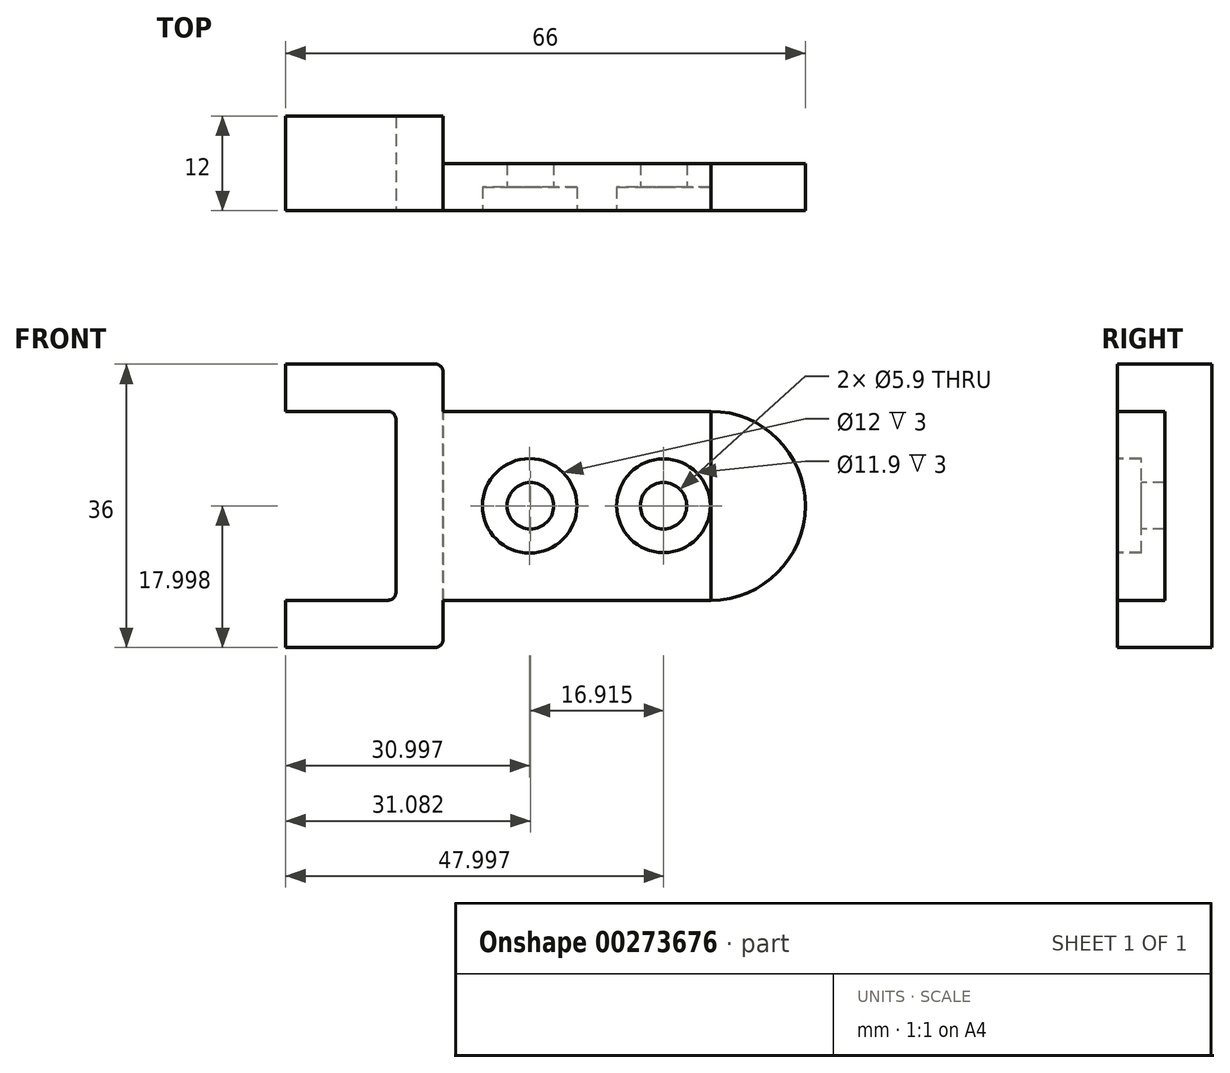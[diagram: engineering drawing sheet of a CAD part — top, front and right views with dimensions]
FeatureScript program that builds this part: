
annotation { "Feature Type Name" : "Feature", "Feature Type Description" : "" }
export const myFeature = defineFeature(function(context is Context, id is Id, definition is map)
    precondition{}
    {
        {
            var Q0;
            Q0=qCreatedBy(makeId("Front.planeOp"),FACE);
            var sketch = newSketch(context, id + "F0", { "sketchPlane" : qUnion([Q0])});
            skLineSegment(sketch, "E0.bottom", {"start": v(-41.74, 12.9) * mm, "end": v(-21.74, 12.9) * mm});
            skLineSegment(sketch, "E0.top", {"start": v(-41.74, -23.1) * mm, "end": v(-21.74, -23.1) * mm});
            skLineSegment(sketch, "E0.left", {"start": v(-41.74, 12.9) * mm, "end": v(-41.74, -23.1) * mm});
            skLineSegment(sketch, "E0.right", {"start": v(-21.74, 12.9) * mm, "end": v(-21.74, -23.1) * mm});
            skSolve(sketch);
        }
        {
            var Q0;
            Q0=makeQuery(id+"F0.imprint","IMPRINT",FACE,{"disambiguationData":[TD([[makeQuery(id+"F0.imprint","IMPRINT",EDGE,{"derivedFrom":sQuery(id+"F0.wireOp",EDGE,"E0.bottom")}),-1.0]])]});
            extrude(context, id + "F1", {"entities" : qUnion([Q0]), "depth" : 12 * mm});
        }
        {
            var Q0;
            Q0=makeQuery(id+"F1.opExtrude","SWEPT_FACE",FACE,{"disambiguationData":[OSD([sQuery(id+"F0.wireOp",EDGE,"E0.left")])]});
            var sketch = newSketch(context, id + "F2", { "sketchPlane" : qUnion([Q0])});
            skLineSegment(sketch, "E1.bottom", {"start": v(0, -17.1) * mm, "end": v(12, -17.1) * mm});
            skLineSegment(sketch, "E1.top", {"start": v(0, 6.9) * mm, "end": v(12, 6.9) * mm});
            skLineSegment(sketch, "E1.left", {"start": v(0, -17.1) * mm, "end": v(0, 6.9) * mm});
            skLineSegment(sketch, "E1.right", {"start": v(12, -17.1) * mm, "end": v(12, 6.9) * mm});
            skPoint(sketch, "E1.middle", {"position": v(6, -5.1) * mm});
            skPoint(sketch, "E1.middle.positionSnap0", {"position": v(12, -5.1) * mm});
            skPoint(sketch, "E1.middle.positionSnap1", {"position": v(6, -23.1) * mm});
            skPoint(sketch, "E1.centerSnap0", {"position": v(12, -5.1) * mm});
            skPoint(sketch, "E1.centerSnap1", {"position": v(6, -23.1) * mm});
            skSolve(sketch);
        }
        {
            var Q0;
            Q0=makeQuery(id+"F2.imprint","IMPRINT",FACE,{"disambiguationData":[TD([[makeQuery(id+"F2.imprint","IMPRINT",EDGE,{"derivedFrom":sQuery(id+"F2.wireOp",EDGE,"E1.bottom")}),1.0]])]});
            extrude(context, id + "F3", {"entities" : qUnion([Q0]), "operationType" : NewBodyOperationType.REMOVE, "oppositeDirection" : true, "depth" : 14 * mm});
        }
        {
            var Q0;
            Q0=qCreatedBy(makeId("Right.planeOp"),FACE);
            var sketch = newSketch(context, id + "F4", { "sketchPlane" : qUnion([Q0])});
            skLineSegment(sketch, "E2", {"start": v(-12.14, -23.1) * mm, "end": v(-12.14, -17.1) * mm});
            skLineSegment(sketch, "E3", {"start": v(-12.14, 12.8) * mm, "end": v(-12.14, 6.8) * mm});
            skLineSegment(sketch, "E4.bottom", {"start": v(-12.14, -17.1) * mm, "end": v(-6.14, -17.1) * mm});
            skLineSegment(sketch, "E4.top", {"start": v(-12.14, 6.8) * mm, "end": v(-6.14, 6.8) * mm});
            skLineSegment(sketch, "E4.left", {"start": v(-12.14, -17.1) * mm, "end": v(-12.14, 6.8) * mm});
            skLineSegment(sketch, "E4.right", {"start": v(-6.14, -17.1) * mm, "end": v(-6.14, 6.8) * mm});
            skSolve(sketch);
        }
        {
            var Q0;
            Q0=makeQuery(id+"F4.imprint","IMPRINT",FACE,{"disambiguationData":[TD([[makeQuery(id+"F4.imprint","IMPRINT",EDGE,{"derivedFrom":sQuery(id+"F4.wireOp",EDGE,"E4.bottom")}),1.0]])]});
            extrude(context, id + "F5", {"entities" : qUnion([Q0]), "depth" : 34 * mm});
        }
        {
            var Q0;
            Q0=makeQuery(id+"F5.opExtrude","SWEPT_BODY",BODY,{"disambiguationData":[OSD([sQuery(id+"F4.wireOp",EDGE,"E4.bottom"),sQuery(id+"F4.wireOp",EDGE,"E4.top"),sQuery(id+"F4.wireOp",EDGE,"E4.left"),sQuery(id+"F4.wireOp",EDGE,"E4.right")])]});
            deleteBodies(context, id + "F6", {"entities" : qUnion([Q0])});
        }
        {
            var Q0;
            Q0=makeQuery(id+"F1.opExtrude","SWEPT_FACE",FACE,{"disambiguationData":[OSD([sQuery(id+"F0.wireOp",EDGE,"E0.right")])]});
            var sketch = newSketch(context, id + "F7", { "sketchPlane" : qUnion([Q0])});
            skLineSegment(sketch, "E5", {"start": v(-12, -17.1) * mm, "end": v(-12, 6.9) * mm});
            skLineSegment(sketch, "E6", {"start": v(-12, -17.1) * mm, "end": v(-6, -17.1) * mm});
            skLineSegment(sketch, "E7", {"start": v(-12, 6.9) * mm, "end": v(-6, 6.9) * mm});
            skLineSegment(sketch, "E8", {"start": v(-6, -17.1) * mm, "end": v(-6, 6.9) * mm});
            skSolve(sketch);
        }
        {
            var Q0;
            Q0=makeQuery(id+"F7.imprint","IMPRINT",FACE,{"disambiguationData":[TD([[makeQuery(id+"F7.imprint","IMPRINT",EDGE,{"derivedFrom":sQuery(id+"F7.wireOp",EDGE,"E5")}),1.0]])]});
            extrude(context, id + "F8", {"entities" : qUnion([Q0]), "operationType" : NewBodyOperationType.ADD, "depth" : 34 * mm});
        }
        {
            var Q0;
            Q0=makeQuery(id+"F8.opExtrude","SWEPT_FACE",FACE,{"disambiguationData":[OSD([sQuery(id+"F7.wireOp",EDGE,"E8")])]});
            var sketch = newSketch(context, id + "F9", { "sketchPlane" : qUnion([Q0])});
            skArc(sketch, "E9", {"start": v(-12.26, 6.9) * mm, "mid": v(-24.26, -5.1) * mm, "end": v(-12.26, -17.1) * mm});
            skSolve(sketch);
        }
        {
            var Q0;
            Q0=makeQuery(id+"F9.imprint","IMPRINT",FACE,{"disambiguationData":[TD([[makeQuery(id+"F9.imprint","IMPRINT",EDGE,{"derivedFrom":sQuery(id+"F9.wireOp",EDGE,"E9")}),1.0]])]});
            extrude(context, id + "F10", {"entities" : qUnion([Q0]), "oppositeDirection" : true, "depth" : 6 * mm});
        }
        {
            var Q0;
            Q0=makeQuery(id+"F8.boolean.opBoolean","MERGE",FACE,{"derivedFrom":[makeQuery(id+"F1.opExtrude","CAP_FACE",FACE,{"disambiguationData":[OSD([sQuery(id+"F0.wireOp",EDGE,"E0.bottom"),sQuery(id+"F0.wireOp",EDGE,"E0.top"),sQuery(id+"F0.wireOp",EDGE,"E0.left"),sQuery(id+"F0.wireOp",EDGE,"E0.right")])],"isStart":false}),makeQuery(id+"F8.opExtrude","SWEPT_FACE",FACE,{"disambiguationData":[OSD([sQuery(id+"F7.wireOp",EDGE,"E5")])]})]});
            var sketch = newSketch(context, id + "F11", { "sketchPlane" : qUnion([Q0])});
            skCircle(sketch, "E10", {"center": v(-10.74, -5.1) * mm, "radius": 6 * mm});
            skPoint(sketch, "E11.orphan", {"position": v(-27.74, -5.1) * mm});
            skSolve(sketch);
        }
        {
            var Q0;
            Q0=makeQuery(id+"F11.imprint","IMPRINT",FACE,{"disambiguationData":[TD([[makeQuery(id+"F11.imprint","IMPRINT",EDGE,{"derivedFrom":sQuery(id+"F11.wireOp",EDGE,"E10")}),1.0]])]});
            extrude(context, id + "F12", {"entities" : qUnion([Q0]), "operationType" : NewBodyOperationType.REMOVE, "oppositeDirection" : true, "depth" : 3 * mm});
        }
        {
            var Q0;
            Q0=makeQuery(id+"F8.boolean.opBoolean","MERGE",FACE,{"derivedFrom":[makeQuery(id+"F1.opExtrude","CAP_FACE",FACE,{"disambiguationData":[OSD([sQuery(id+"F0.wireOp",EDGE,"E0.bottom"),sQuery(id+"F0.wireOp",EDGE,"E0.top"),sQuery(id+"F0.wireOp",EDGE,"E0.left"),sQuery(id+"F0.wireOp",EDGE,"E0.right")])],"isStart":false}),makeQuery(id+"F8.opExtrude","SWEPT_FACE",FACE,{"disambiguationData":[OSD([sQuery(id+"F7.wireOp",EDGE,"E5")])]})]});
            var sketch = newSketch(context, id + "F13", { "sketchPlane" : qUnion([Q0])});
            skPoint(sketch, "E12.orphan", {"position": v(-10.74, -5.1) * mm});
            skLineSegment(sketch, "E13", {"start": v(-10.74, -5.1) * mm, "end": v(6.26, -5.1) * mm});
            skCircle(sketch, "E14", {"center": v(6.26, -5.1) * mm, "radius": 5.95 * mm});
            skSolve(sketch);
        }
        {
            var Q0;
            Q0=makeQuery(id+"F13.imprint","IMPRINT",FACE,{"disambiguationData":[TD([[makeQuery(id+"F13.imprint","IMPRINT",EDGE,{"derivedFrom":sQuery(id+"F13.wireOp",EDGE,"E14")}),1.0]])]});
            extrude(context, id + "F14", {"entities" : qUnion([Q0]), "operationType" : NewBodyOperationType.REMOVE, "oppositeDirection" : true, "depth" : 3 * mm});
        }
        {
            var Q0;
            Q0=makeQuery(id+"F14.boolean.opBoolean","COPY",FACE,{"derivedFrom":makeQuery(id+"F14.opExtrude","CAP_FACE",FACE,{"disambiguationData":[OSD([sQuery(id+"F13.wireOp",EDGE,"E14")])],"isStart":false})});
            var sketch = newSketch(context, id + "F15", { "sketchPlane" : qUnion([Q0])});
            skCircle(sketch, "E15", {"center": v(6.26, -5.1) * mm, "radius": 2.95 * mm});
            skCircle(sketch, "E16", {"center": v(-10.66, -5.1) * mm, "radius": 2.95 * mm});
            skSolve(sketch);
        }
        {
            var Q0;
            Q0=sQuery(id+"F15.wireOp",VERTEX,"E15.center");
            var Q1;
            Q1=sQuery(id+"F15.wireOp",VERTEX,"E16.center");
            var Q2;
            Q2=makeQuery(id+"F1.opExtrude","SWEPT_BODY",BODY,{"disambiguationData":[OSD([sQuery(id+"F0.wireOp",EDGE,"E0.bottom"),sQuery(id+"F0.wireOp",EDGE,"E0.top"),sQuery(id+"F0.wireOp",EDGE,"E0.left"),sQuery(id+"F0.wireOp",EDGE,"E0.right")])]});
            hole(context, id + "F16", {"style" : HoleStyle.SIMPLE, "endStyle" : HoleEndStyle.THROUGH, "holeDiameter" : 5.9 * mm, "tappedDepth" : 12 * mm, "tapClearance" : 3, "locations" : qUnion([Q0, Q1]), "scope" : qUnion([Q2])});
        }
        {
            var Q0;
            Q0=makeQuery(id+"F3.boolean.opBoolean","COPY",EDGE,{"derivedFrom":makeQuery(id+"F3.opExtrude","CAP_EDGE",EDGE,{"disambiguationData":[OSD([sQuery(id+"F2.wireOp",EDGE,"E1.top")])],"isStart":false})});
            var Q1;
            Q1=makeQuery(id+"F3.boolean.opBoolean","COPY",EDGE,{"derivedFrom":makeQuery(id+"F3.opExtrude","CAP_EDGE",EDGE,{"disambiguationData":[OSD([sQuery(id+"F2.wireOp",EDGE,"E1.bottom")])],"isStart":false})});
            var Q2;
            Q2=makeQuery(id+"F1.opExtrude","SWEPT_EDGE",EDGE,{"disambiguationData":[OSD([sQuery(id+"F0.wireOp",EDGE,"E0.bottom"),sQuery(id+"F0.wireOp",EDGE,"E0.right")])]});
            var Q3;
            Q3=makeQuery(id+"F1.opExtrude","SWEPT_EDGE",EDGE,{"disambiguationData":[OSD([sQuery(id+"F0.wireOp",EDGE,"E0.top"),sQuery(id+"F0.wireOp",EDGE,"E0.right")])]});
            fillet(context, id + "F17", {"entities" : qUnion([Q0, Q1, Q2, Q3]), "radius" : 1 * mm, "tangentPropagation" : true, "allowEdgeOverflow" : false});
        }
    });
